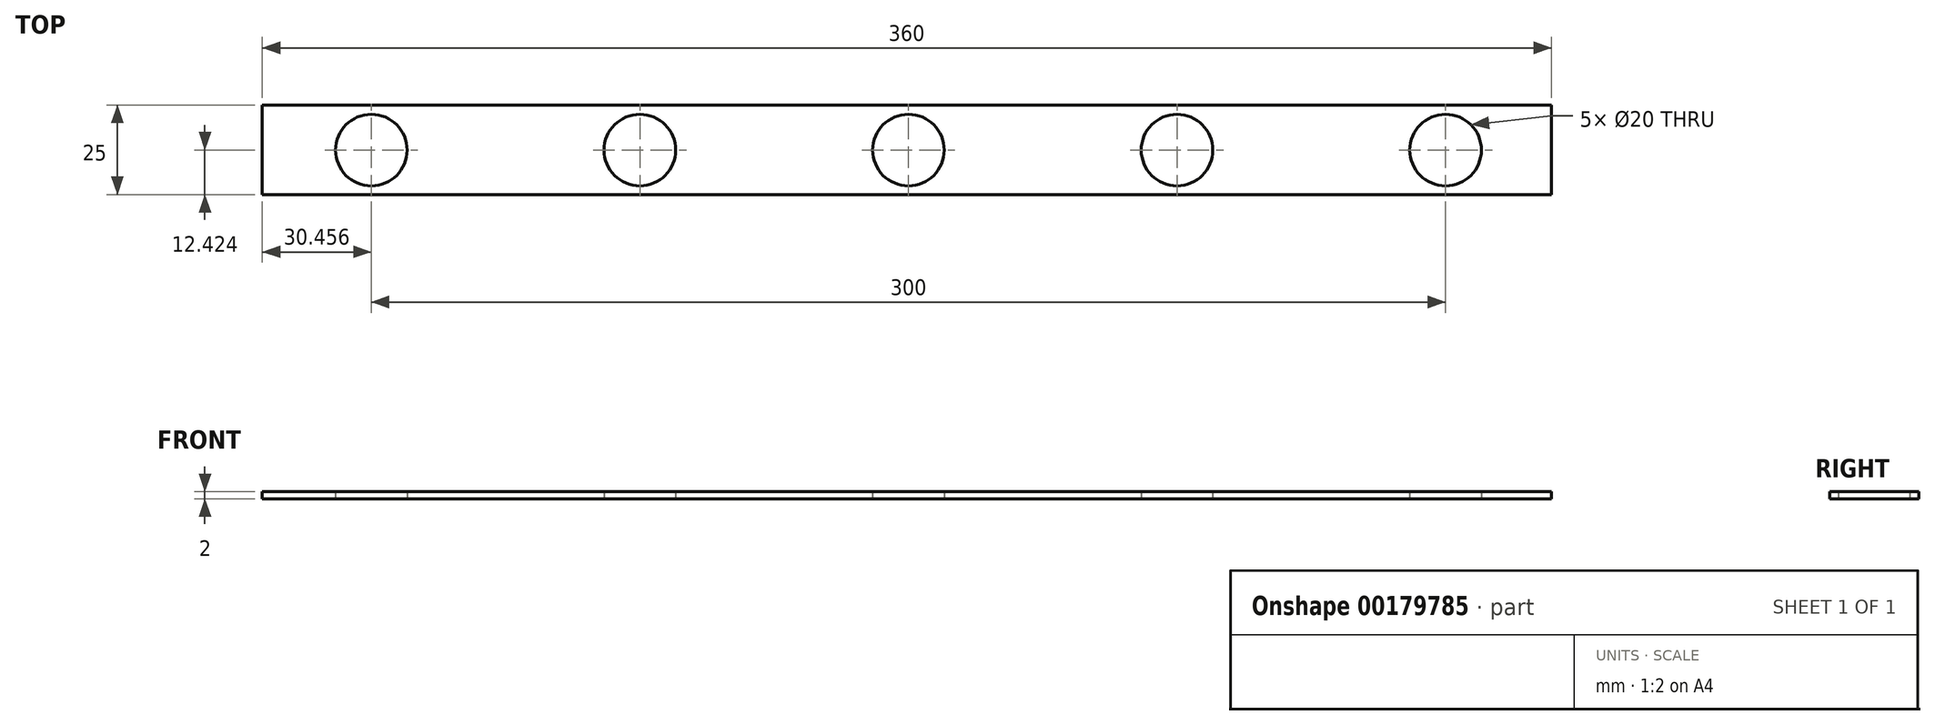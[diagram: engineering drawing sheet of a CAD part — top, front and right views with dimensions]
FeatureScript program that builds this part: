
annotation { "Feature Type Name" : "Feature", "Feature Type Description" : "" }
export const myFeature = defineFeature(function(context is Context, id is Id, definition is map)
    precondition{}
    {
        {
            var Q0;
            Q0=qCreatedBy(makeId("Top.planeOp"),FACE);
            var sketch = newSketch(context, id + "F0", { "sketchPlane" : qUnion([Q0])});
            skLineSegment(sketch, "E0.bottom", {"start": v(180, -12.5) * mm, "end": v(-180, -12.5) * mm});
            skLineSegment(sketch, "E0.top", {"start": v(180, 12.5) * mm, "end": v(-180, 12.5) * mm});
            skLineSegment(sketch, "E0.left", {"start": v(180, -12.5) * mm, "end": v(180, 12.5) * mm});
            skLineSegment(sketch, "E0.right", {"start": v(-180, -12.5) * mm, "end": v(-180, 12.5) * mm});
            skPoint(sketch, "E0.middle", {"position": v(0, 0) * mm});
            skSolve(sketch);
        }
        {
            var Q0;
            Q0 = qSketchRegion(id + "F0", true);
            extrude(context, id + "F1", {"entities" : qUnion([Q0]), "depth" : 2 * mm});
        }
        {
            var Q0;
            Q0=qCreatedBy(makeId("Top.planeOp"),FACE);
            var sketch = newSketch(context, id + "F2", { "sketchPlane" : qUnion([Q0])});
            skCircle(sketch, "E1", {"center": v(-149.54, -0.08) * mm, "radius": 10 * mm});
            skCircle(sketch, "E2", {"center": v(-74.54, -0.08) * mm, "radius": 10 * mm});
            skCircle(sketch, "E3", {"center": v(0.46, -0.08) * mm, "radius": 10 * mm});
            skCircle(sketch, "E4", {"center": v(75.46, -0.08) * mm, "radius": 10 * mm});
            skCircle(sketch, "E5", {"center": v(150.46, -0.08) * mm, "radius": 10 * mm});
            skSolve(sketch);
        }
        {
            var Q0;
            Q0=sQuery(id+"F2.wireOp",VERTEX,"E1.center");
            var Q1;
            Q1=sQuery(id+"F2.wireOp",VERTEX,"E2.center");
            var Q2;
            Q2=sQuery(id+"F2.wireOp",VERTEX,"E3.center");
            var Q3;
            Q3=sQuery(id+"F2.wireOp",VERTEX,"E4.center");
            var Q4;
            Q4=sQuery(id+"F2.wireOp",VERTEX,"E5.center");
            var Q5;
            Q5=makeQuery(id+"F1.opExtrude","SWEPT_BODY",BODY,{"disambiguationData":[OSD([sQuery(id+"F0.wireOp",EDGE,"E0.bottom"),sQuery(id+"F0.wireOp",EDGE,"E0.top"),sQuery(id+"F0.wireOp",EDGE,"E0.left"),sQuery(id+"F0.wireOp",EDGE,"E0.right")])]});
            hole(context, id + "F3", {"style" : HoleStyle.SIMPLE, "endStyle" : HoleEndStyle.THROUGH, "oppositeDirection" : true, "holeDiameter" : 20 * mm, "locations" : qUnion([Q0, Q1, Q2, Q3, Q4]), "scope" : qUnion([Q5]), "isTappedThrough" : true});
        }
    });
